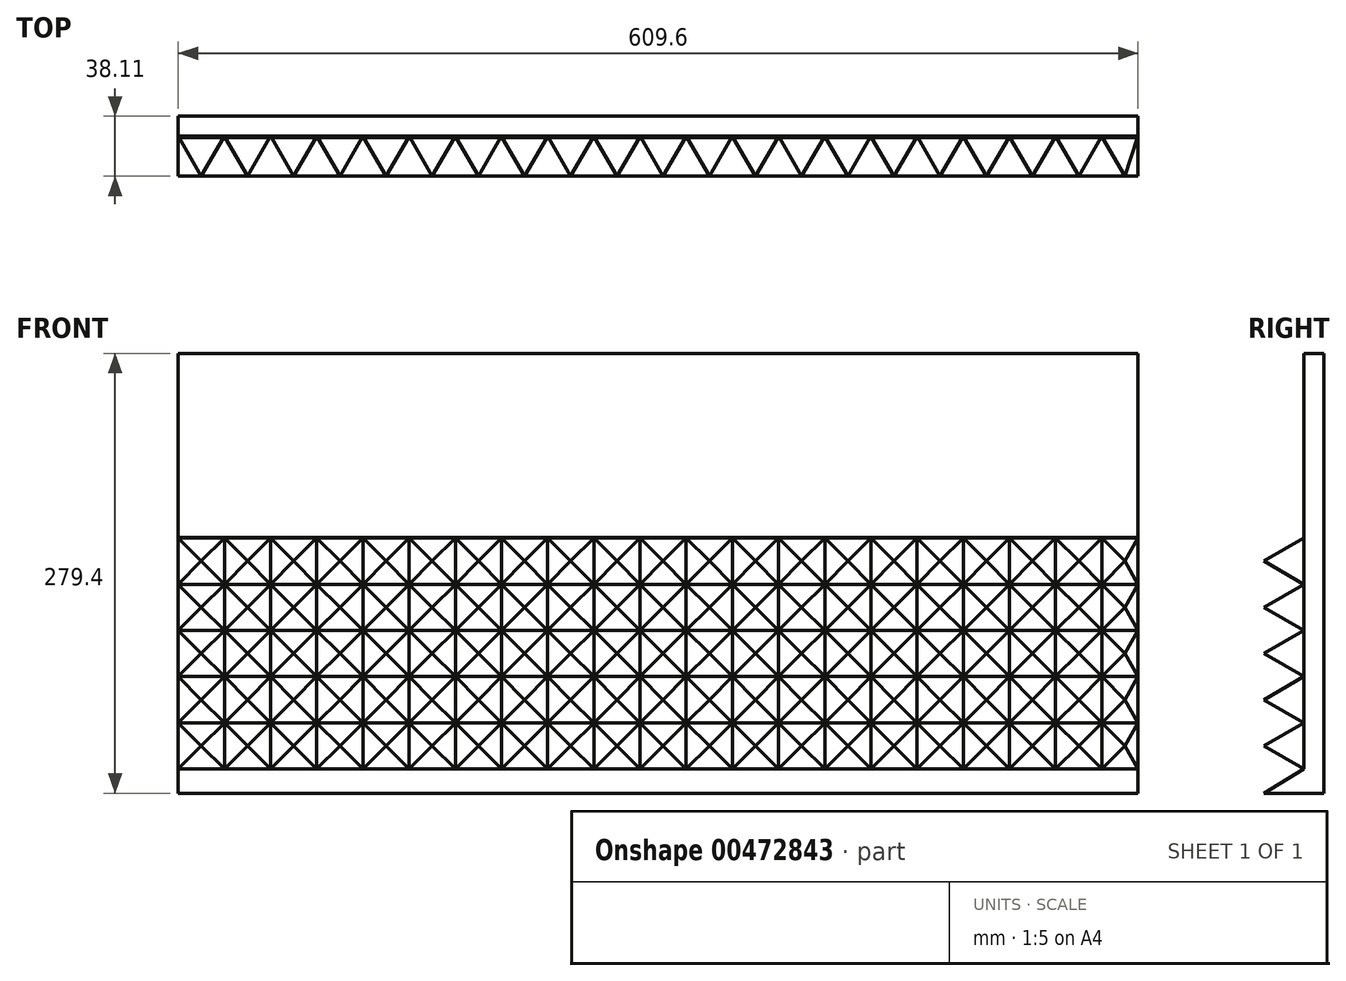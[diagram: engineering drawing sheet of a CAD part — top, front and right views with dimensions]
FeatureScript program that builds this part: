
annotation { "Feature Type Name" : "Feature", "Feature Type Description" : "" }
export const myFeature = defineFeature(function(context is Context, id is Id, definition is map)
    precondition{}
    {
        {
            var Q0;
            Q0=qCreatedBy(makeId("Front.planeOp"),FACE);
            var sketch = newSketch(context, id + "F0", { "sketchPlane" : qUnion([Q0])});
            skLineSegment(sketch, "E0.bottom", {"start": v(304.8, 139.7) * mm, "end": v(-304.8, 139.7) * mm});
            skLineSegment(sketch, "E0.top", {"start": v(304.8, -139.7) * mm, "end": v(-304.8, -139.7) * mm});
            skLineSegment(sketch, "E0.left", {"start": v(304.8, 139.7) * mm, "end": v(304.8, -139.7) * mm});
            skLineSegment(sketch, "E0.right", {"start": v(-304.8, 139.7) * mm, "end": v(-304.8, -139.7) * mm});
            skPoint(sketch, "E0.middle", {"position": v(0, 0) * mm});
            skSolve(sketch);
        }
        {
            var Q0;
            Q0=makeQuery(id+"F0.imprint","IMPRINT",FACE,{"disambiguationData":[TD([[makeQuery(id+"F0.imprint","IMPRINT",EDGE,{"derivedFrom":sQuery(id+"F0.wireOp",EDGE,"E0.bottom")}),1.0]])]});
            extrude(context, id + "F1", {"entities" : qUnion([Q0]), "depth" : 25.4 * mm});
        }
        {
            var Q0;
            Q0=makeQuery(id+"F1.opExtrude","SWEPT_FACE",FACE,{"disambiguationData":[OSD([sQuery(id+"F0.wireOp",EDGE,"E0.bottom")])]});
            var sketch = newSketch(context, id + "F2", { "sketchPlane" : qUnion([Q0])});
            skLineSegment(sketch, "E1", {"start": v(-304.8, 0) * mm, "end": v(-290.14, -25.4) * mm});
            skLineSegment(sketch, "E2", {"start": v(-290.14, -25.4) * mm, "end": v(-275.47, 0) * mm});
            skLineSegment(sketch, "E3", {"start": v(-275.47, 0) * mm, "end": v(-260.8, -25.4) * mm});
            skLineSegment(sketch, "E4", {"start": v(-260.8, -25.4) * mm, "end": v(-246.14, 0) * mm});
            skLineSegment(sketch, "E5", {"start": v(-246.14, 0) * mm, "end": v(-231.48, -25.4) * mm});
            skLineSegment(sketch, "E6", {"start": v(-231.48, -25.4) * mm, "end": v(-216.81, 0) * mm});
            skLineSegment(sketch, "E7", {"start": v(-216.81, 0) * mm, "end": v(-202.15, -25.4) * mm});
            skLineSegment(sketch, "E8", {"start": v(-202.15, -25.4) * mm, "end": v(-187.48, 0) * mm});
            skLineSegment(sketch, "E9", {"start": v(-187.48, 0) * mm, "end": v(-172.82, -25.4) * mm});
            skLineSegment(sketch, "E10", {"start": v(-172.82, -25.4) * mm, "end": v(-158.15, 0) * mm});
            skLineSegment(sketch, "E11", {"start": v(-158.15, 0) * mm, "end": v(-143.49, -25.4) * mm});
            skLineSegment(sketch, "E12", {"start": v(-143.49, -25.4) * mm, "end": v(-128.82, 0) * mm});
            skLineSegment(sketch, "E13", {"start": v(-128.82, 0) * mm, "end": v(-114.16, -25.4) * mm});
            skLineSegment(sketch, "E14", {"start": v(-114.16, -25.4) * mm, "end": v(-99.5, 0) * mm});
            skLineSegment(sketch, "E15", {"start": v(-99.5, 0) * mm, "end": v(-84.83, -25.4) * mm});
            skLineSegment(sketch, "E16", {"start": v(-84.83, -25.4) * mm, "end": v(-70.16, 0) * mm});
            skLineSegment(sketch, "E17", {"start": v(-70.16, 0) * mm, "end": v(-55.5, -25.4) * mm});
            skLineSegment(sketch, "E18", {"start": v(-55.5, -25.4) * mm, "end": v(-40.84, 0) * mm});
            skLineSegment(sketch, "E19", {"start": v(-40.84, 0) * mm, "end": v(-26.17, -25.4) * mm});
            skLineSegment(sketch, "E20", {"start": v(-26.17, -25.4) * mm, "end": v(-11.5, 0) * mm});
            skLineSegment(sketch, "E21", {"start": v(-11.5, 0) * mm, "end": v(3.16, -25.4) * mm});
            skLineSegment(sketch, "E22", {"start": v(3.16, -25.4) * mm, "end": v(17.82, 0) * mm});
            skLineSegment(sketch, "E23", {"start": v(17.82, 0) * mm, "end": v(32.49, -25.4) * mm});
            skLineSegment(sketch, "E24", {"start": v(32.49, -25.4) * mm, "end": v(47.15, 0) * mm});
            skLineSegment(sketch, "E25", {"start": v(47.15, 0) * mm, "end": v(61.82, -25.4) * mm});
            skLineSegment(sketch, "E26", {"start": v(61.82, -25.4) * mm, "end": v(76.48, 0) * mm});
            skLineSegment(sketch, "E27", {"start": v(304.8, -47.17) * mm, "end": v(304.8, 0) * mm});
            skLineSegment(sketch, "E28", {"start": v(76.48, 0) * mm, "end": v(91.15, -25.4) * mm});
            skLineSegment(sketch, "E29", {"start": v(304.8, -47.17) * mm, "end": v(-304.8, -47.17) * mm});
            skLineSegment(sketch, "E30", {"start": v(-304.8, -47.17) * mm, "end": v(-304.8, 0) * mm});
            skLineSegment(sketch, "E31", {"start": v(91.15, -25.4) * mm, "end": v(105.81, 0) * mm});
            skLineSegment(sketch, "E32", {"start": v(105.81, 0) * mm, "end": v(120.48, -25.4) * mm});
            skLineSegment(sketch, "E33", {"start": v(120.48, -25.4) * mm, "end": v(135.14, 0) * mm});
            skLineSegment(sketch, "E34", {"start": v(135.14, 0) * mm, "end": v(149.8, -25.4) * mm});
            skLineSegment(sketch, "E35", {"start": v(149.8, -25.4) * mm, "end": v(164.47, 0) * mm});
            skLineSegment(sketch, "E36", {"start": v(164.47, 0) * mm, "end": v(179.13, -25.4) * mm});
            skLineSegment(sketch, "E37", {"start": v(179.13, -25.4) * mm, "end": v(193.8, 0) * mm});
            skLineSegment(sketch, "E38", {"start": v(193.8, 0) * mm, "end": v(208.46, -25.4) * mm});
            skLineSegment(sketch, "E39", {"start": v(208.46, -25.4) * mm, "end": v(223.13, 0) * mm});
            skLineSegment(sketch, "E40", {"start": v(223.13, 0) * mm, "end": v(237.8, -25.4) * mm});
            skLineSegment(sketch, "E41", {"start": v(237.8, -25.4) * mm, "end": v(252.46, 0) * mm});
            skLineSegment(sketch, "E42", {"start": v(252.46, 0) * mm, "end": v(267.12, -25.4) * mm});
            skLineSegment(sketch, "E43", {"start": v(267.12, -25.4) * mm, "end": v(281.79, 0) * mm});
            skLineSegment(sketch, "E44", {"start": v(281.79, 0) * mm, "end": v(296.45, -25.4) * mm});
            skLineSegment(sketch, "E45", {"start": v(296.45, -25.4) * mm, "end": v(304.8, 0) * mm});
            skSolve(sketch);
        }
        {
            var Q0;
            Q0 = qSketchRegion(id + "F2", true);
            extrude(context, id + "F3", {"entities" : qUnion([Q0]), "operationType" : NewBodyOperationType.REMOVE, "endBound" : BoundingType.THROUGH_ALL, "oppositeDirection" : true, "depth" : 25.4 * mm, "offsetDistance" : 25.4 * mm});
        }
        {
            var Q0;
            Q0=qCreatedBy(makeId("Right.planeOp"),FACE);
            var sketch = newSketch(context, id + "F4", { "sketchPlane" : qUnion([Q0])});
            skPoint(sketch, "E46.0", {"position": v(0, 139.7) * mm});
            skPoint(sketch, "E47.0", {"position": v(0, -139.7) * mm});
            skLineSegment(sketch, "E48.0", {"start": v(-25.4, -139.7) * mm, "end": v(-25.4, 139.7) * mm, "construction": true});
            skLineSegment(sketch, "E49", {"start": v(0, 139.7) * mm, "end": v(-25.4, 125.04) * mm});
            skLineSegment(sketch, "E50", {"start": v(-25.4, 125.04) * mm, "end": v(0, 110.37) * mm});
            skLineSegment(sketch, "E51", {"start": v(0, 110.37) * mm, "end": v(-25.4, 95.7) * mm});
            skLineSegment(sketch, "E52", {"start": v(-25.4, 95.7) * mm, "end": v(0, 81.04) * mm});
            skLineSegment(sketch, "E53", {"start": v(0, 81.04) * mm, "end": v(-25.4, 66.38) * mm});
            skLineSegment(sketch, "E54", {"start": v(-25.4, 66.38) * mm, "end": v(0, 51.71) * mm});
            skLineSegment(sketch, "E55", {"start": v(0, 51.71) * mm, "end": v(-25.4, 37.05) * mm});
            skLineSegment(sketch, "E56", {"start": v(-25.4, 37.05) * mm, "end": v(0, 22.38) * mm});
            skLineSegment(sketch, "E57", {"start": v(0, 22.38) * mm, "end": v(-25.4, 7.72) * mm});
            skLineSegment(sketch, "E58", {"start": v(-25.4, 7.72) * mm, "end": v(0, -6.95) * mm});
            skLineSegment(sketch, "E59", {"start": v(0, -6.95) * mm, "end": v(-25.4, -21.61) * mm});
            skLineSegment(sketch, "E60", {"start": v(-25.4, -21.61) * mm, "end": v(0, -36.28) * mm});
            skLineSegment(sketch, "E61", {"start": v(0, -36.28) * mm, "end": v(-25.4, -50.94) * mm});
            skLineSegment(sketch, "E62", {"start": v(-25.4, -50.94) * mm, "end": v(0, -65.6) * mm});
            skLineSegment(sketch, "E63", {"start": v(0, -65.6) * mm, "end": v(-25.4, -80.27) * mm});
            skLineSegment(sketch, "E64", {"start": v(-25.4, -80.27) * mm, "end": v(0, -94.94) * mm});
            skLineSegment(sketch, "E65", {"start": v(0, -94.94) * mm, "end": v(-25.4, -109.6) * mm});
            skLineSegment(sketch, "E66", {"start": v(-25.4, -109.6) * mm, "end": v(0, -124.26) * mm});
            skLineSegment(sketch, "E67", {"start": v(0, -124.26) * mm, "end": v(-25.4, -139.7) * mm});
            skLineSegment(sketch, "E68", {"start": v(-54.92, 139.7) * mm, "end": v(-54.92, -139.7) * mm});
            skLineSegment(sketch, "E69", {"start": v(-54.92, 139.7) * mm, "end": v(0, 139.7) * mm});
            skLineSegment(sketch, "E70", {"start": v(-54.92, -139.7) * mm, "end": v(0, -139.7) * mm});
            skSolve(sketch);
        }
        {
            var Q0;
            Q0=qCreatedBy(makeId("Front.planeOp"),FACE);
            var sketch = newSketch(context, id + "F5", { "sketchPlane" : qUnion([Q0])});
            skLineSegment(sketch, "E71.bottom", {"start": v(-304.8, 139.7) * mm, "end": v(304.8, 139.7) * mm});
            skLineSegment(sketch, "E71.top", {"start": v(-304.8, -139.7) * mm, "end": v(304.8, -139.7) * mm});
            skLineSegment(sketch, "E71.left", {"start": v(-304.8, 139.7) * mm, "end": v(-304.8, -139.7) * mm});
            skLineSegment(sketch, "E71.right", {"start": v(304.8, 139.7) * mm, "end": v(304.8, -139.7) * mm});
            skPoint(sketch, "E71.middle", {"position": v(0, 0) * mm});
            skSolve(sketch);
        }
        {
            var Q0;
            Q0 = qSketchRegion(id + "F5", true);
            extrude(context, id + "F6", {"entities" : qUnion([Q0]), "operationType" : NewBodyOperationType.ADD, "oppositeDirection" : true, "depth" : 12.7 * mm});
        }
        {
            var Q0;
            Q0=makeQuery(id+"F4.imprint","IMPRINT",FACE,{"disambiguationData":[TD([[makeQuery(id+"F4.imprint","IMPRINT",EDGE,{"derivedFrom":sQuery(id+"F4.wireOp",EDGE,"E49")}),-1.0]])]});
            extrude(context, id + "F7", {"entities" : qUnion([Q0]), "operationType" : NewBodyOperationType.REMOVE, "endBound" : BoundingType.THROUGH_ALL, "oppositeDirection" : true, "depth" : 25.4 * mm, "hasSecondDirection" : true, "secondDirectionBound" : SecondDirectionBoundingType.THROUGH_ALL, "secondDirectionOppositeDirection" : false, "secondDirectionDepth" : 25.4 * mm});
        }
        {
            var Q0;
            Q0=qCreatedBy(makeId("Right.planeOp"),FACE);
            var sketch = newSketch(context, id + "F8", { "sketchPlane" : qUnion([Q0])});
            skLineSegment(sketch, "E72.0", {"start": v(0, -124.26) * mm, "end": v(-25.4, -139.7) * mm});
            skLineSegment(sketch, "E73.0", {"start": v(0, -139.7) * mm, "end": v(-25.4, -139.7) * mm});
            skLineSegment(sketch, "E74", {"start": v(0, -139.7) * mm, "end": v(12.71, -139.7) * mm});
            skLineSegment(sketch, "E75", {"start": v(12.71, -139.7) * mm, "end": v(12.71, -124.26) * mm});
            skLineSegment(sketch, "E76", {"start": v(12.71, -124.26) * mm, "end": v(0, -124.26) * mm});
            skSolve(sketch);
        }
        {
            var Q0;
            Q0=makeQuery(id+"F8.imprint","IMPRINT",FACE,{"disambiguationData":[TD([[makeQuery(id+"F8.imprint","IMPRINT",EDGE,{"derivedFrom":sQuery(id+"F8.wireOp",EDGE,"E72.0")}),1.0]])]});
            extrude(context, id + "F9", {"entities" : qUnion([Q0]), "operationType" : NewBodyOperationType.ADD, "depth" : 304.8 * mm, "hasSecondDirection" : true, "secondDirectionOppositeDirection" : true, "secondDirectionDepth" : 304.8 * mm, "offsetDistance" : 25.4 * mm});
        }
        {
            var Q0;
            {var subQ0=sQuery(id+"F0.wireOp",EDGE,"E0.bottom");var subQ2=makeQuery(id+"F1.opExtrude","SWEPT_FACE",FACE,{"disambiguationData":[OSD([subQ0])]});Q0=makeQuery(id+"F6.boolean.opBoolean","MERGE",FACE,{"derivedFrom":[makeQuery(id+"F3.boolean.opBoolean","SPLIT",FACE,{"disambiguationData":[TD([makeQuery(id+"F3.opExtrude","SWEPT_FACE",FACE,{"disambiguationData":[OSD([sQuery(id+"F2.wireOp",EDGE,"E1")])]})])],"derivedFrom":subQ2}),makeQuery(id+"F3.boolean.opBoolean","SPLIT",FACE,{"disambiguationData":[TD([makeQuery(id+"F3.opExtrude","SWEPT_FACE",FACE,{"disambiguationData":[OSD([sQuery(id+"F2.wireOp",EDGE,"E3")])]})])],"derivedFrom":subQ2}),makeQuery(id+"F3.boolean.opBoolean","SPLIT",FACE,{"disambiguationData":[TD([makeQuery(id+"F3.opExtrude","SWEPT_FACE",FACE,{"disambiguationData":[OSD([sQuery(id+"F2.wireOp",EDGE,"E5")])]})])],"derivedFrom":subQ2}),makeQuery(id+"F3.boolean.opBoolean","SPLIT",FACE,{"disambiguationData":[TD([makeQuery(id+"F3.opExtrude","SWEPT_FACE",FACE,{"disambiguationData":[OSD([sQuery(id+"F2.wireOp",EDGE,"E7")])]})])],"derivedFrom":subQ2}),makeQuery(id+"F3.boolean.opBoolean","SPLIT",FACE,{"disambiguationData":[TD([makeQuery(id+"F3.opExtrude","SWEPT_FACE",FACE,{"disambiguationData":[OSD([sQuery(id+"F2.wireOp",EDGE,"E9")])]})])],"derivedFrom":subQ2}),makeQuery(id+"F3.boolean.opBoolean","SPLIT",FACE,{"disambiguationData":[TD([makeQuery(id+"F3.opExtrude","SWEPT_FACE",FACE,{"disambiguationData":[OSD([sQuery(id+"F2.wireOp",EDGE,"E11")])]})])],"derivedFrom":subQ2}),makeQuery(id+"F3.boolean.opBoolean","SPLIT",FACE,{"disambiguationData":[TD([makeQuery(id+"F3.opExtrude","SWEPT_FACE",FACE,{"disambiguationData":[OSD([sQuery(id+"F2.wireOp",EDGE,"E13")])]})])],"derivedFrom":subQ2}),makeQuery(id+"F3.boolean.opBoolean","SPLIT",FACE,{"disambiguationData":[TD([makeQuery(id+"F3.opExtrude","SWEPT_FACE",FACE,{"disambiguationData":[OSD([sQuery(id+"F2.wireOp",EDGE,"E15")])]})])],"derivedFrom":subQ2}),makeQuery(id+"F3.boolean.opBoolean","SPLIT",FACE,{"disambiguationData":[TD([makeQuery(id+"F3.opExtrude","SWEPT_FACE",FACE,{"disambiguationData":[OSD([sQuery(id+"F2.wireOp",EDGE,"E17")])]})])],"derivedFrom":subQ2}),makeQuery(id+"F3.boolean.opBoolean","SPLIT",FACE,{"disambiguationData":[TD([makeQuery(id+"F3.opExtrude","SWEPT_FACE",FACE,{"disambiguationData":[OSD([sQuery(id+"F2.wireOp",EDGE,"E19")])]})])],"derivedFrom":subQ2}),makeQuery(id+"F3.boolean.opBoolean","SPLIT",FACE,{"disambiguationData":[TD([makeQuery(id+"F3.opExtrude","SWEPT_FACE",FACE,{"disambiguationData":[OSD([sQuery(id+"F2.wireOp",EDGE,"E21")])]})])],"derivedFrom":subQ2}),makeQuery(id+"F3.boolean.opBoolean","SPLIT",FACE,{"disambiguationData":[TD([makeQuery(id+"F3.opExtrude","SWEPT_FACE",FACE,{"disambiguationData":[OSD([sQuery(id+"F2.wireOp",EDGE,"E23")])]})])],"derivedFrom":subQ2}),makeQuery(id+"F3.boolean.opBoolean","SPLIT",FACE,{"disambiguationData":[TD([makeQuery(id+"F3.opExtrude","SWEPT_FACE",FACE,{"disambiguationData":[OSD([sQuery(id+"F2.wireOp",EDGE,"E25")])]})])],"derivedFrom":subQ2}),makeQuery(id+"F3.boolean.opBoolean","SPLIT",FACE,{"disambiguationData":[TD([makeQuery(id+"F3.opExtrude","SWEPT_FACE",FACE,{"disambiguationData":[OSD([sQuery(id+"F2.wireOp",EDGE,"E28")])]})])],"derivedFrom":subQ2}),makeQuery(id+"F6.opExtrude","SWEPT_FACE",FACE,{"disambiguationData":[OSD([sQuery(id+"F5.wireOp",EDGE,"E71.bottom")])]})]});}
            var sketch = newSketch(context, id + "F10", { "sketchPlane" : qUnion([Q0])});
            skLineSegment(sketch, "E77.bottom", {"start": v(-304.8, 0) * mm, "end": v(101.6, 0) * mm});
            skLineSegment(sketch, "E78", {"start": v(-304.8, 0) * mm, "end": v(-305.66, 0) * mm});
            skLineSegment(sketch, "E79", {"start": v(-305.66, 0) * mm, "end": v(-305.66, -53.38) * mm});
            skLineSegment(sketch, "E80", {"start": v(-305.66, -53.38) * mm, "end": v(311.33, -53.38) * mm});
            skLineSegment(sketch, "E81", {"start": v(311.33, -53.38) * mm, "end": v(311.33, 0) * mm});
            skLineSegment(sketch, "E82", {"start": v(311.33, 0) * mm, "end": v(101.6, 0) * mm});
            skSolve(sketch);
        }
        {
            var Q0;
            {var subQ8=sQuery(id+"F10.wireOp",EDGE,"E78");Q0=makeQuery(id+"F10.imprint","IMPRINT",FACE,{"disambiguationData":[TD([[makeQuery(id+"F10.imprint","IMPRINT",EDGE,{"derivedFrom":subQ8}),1.0]])]});}
            extrude(context, id + "F11", {"entities" : qUnion([Q0]), "operationType" : NewBodyOperationType.REMOVE, "oppositeDirection" : true, "depth" : 116.84 * mm, "offsetDistance" : 25.4 * mm});
        }
    });
